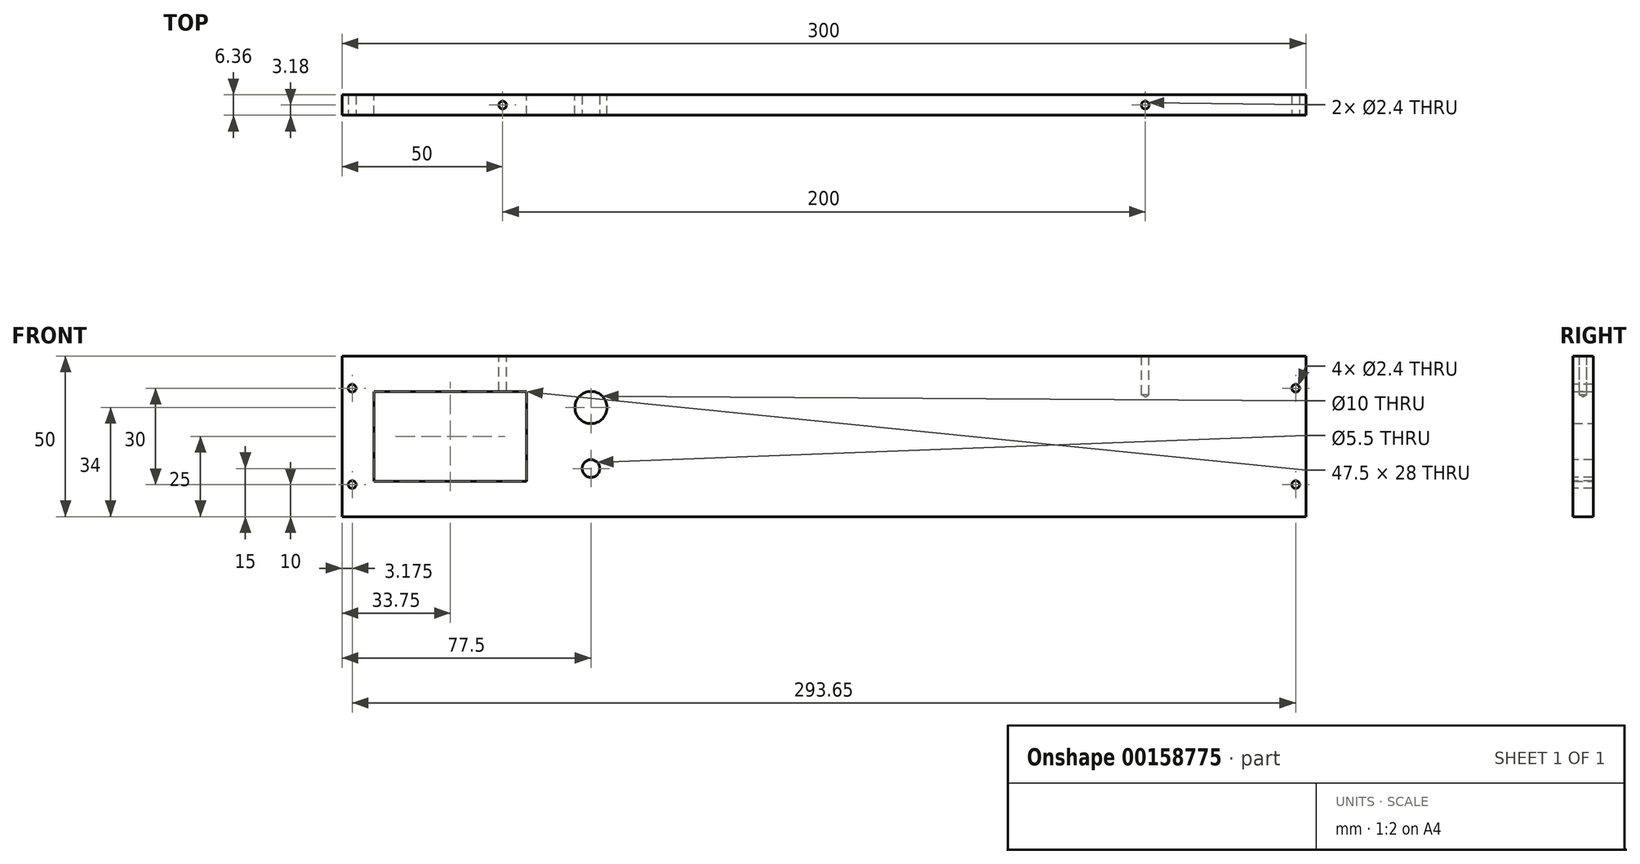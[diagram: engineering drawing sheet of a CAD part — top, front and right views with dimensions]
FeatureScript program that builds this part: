
annotation { "Feature Type Name" : "Feature", "Feature Type Description" : "" }
export const myFeature = defineFeature(function(context is Context, id is Id, definition is map)
    precondition{}
    {
        {
            var Q0;
            Q0=qCreatedBy(makeId("Front.planeOp"),FACE);
            var sketch = newSketch(context, id + "F0", { "sketchPlane" : qUnion([Q0])});
            skLineSegment(sketch, "E0.bottom", {"start": v(150, -25) * mm, "end": v(-150, -25) * mm});
            skLineSegment(sketch, "E0.top", {"start": v(150, 25) * mm, "end": v(-150, 25) * mm});
            skLineSegment(sketch, "E0.left", {"start": v(150, -25) * mm, "end": v(150, 25) * mm});
            skLineSegment(sketch, "E0.right", {"start": v(-150, -25) * mm, "end": v(-150, 25) * mm});
            skPoint(sketch, "E0.middle", {"position": v(0, 0) * mm});
            skLineSegment(sketch, "E1.bottom", {"start": v(-92.5, -14) * mm, "end": v(-140, -14) * mm});
            skLineSegment(sketch, "E1.top", {"start": v(-92.5, 14) * mm, "end": v(-140, 14) * mm});
            skLineSegment(sketch, "E1.left", {"start": v(-92.5, -14) * mm, "end": v(-92.5, 14) * mm});
            skLineSegment(sketch, "E1.right", {"start": v(-140, -14) * mm, "end": v(-140, 14) * mm});
            skPoint(sketch, "E1.middle", {"position": v(-116.25, 0) * mm});
            skCircle(sketch, "E2", {"center": v(-72.5, 9) * mm, "radius": 5 * mm});
            skSolve(sketch);
        }
        {
            var Q0;
            Q0=qSketchRegion(id+"F0",true);
            extrude(context, id + "F1", {"entities" : qUnion([Q0]), "endBound" : BoundingType.SYMMETRIC, "depth" : 6.35 * mm});
        }
        {
            var Q0;
            Q0=makeQuery(id+"F1.opExtrude","CAP_FACE",FACE,{"disambiguationData":[OSD([sQuery(id+"F0.wireOp",EDGE,"E0.bottom"),sQuery(id+"F0.wireOp",EDGE,"E0.top"),sQuery(id+"F0.wireOp",EDGE,"E0.left"),sQuery(id+"F0.wireOp",EDGE,"E0.right")])],"isStart":false});
            var sketch = newSketch(context, id + "F2", { "sketchPlane" : qUnion([Q0])});
            skCircle(sketch, "E3", {"center": v(-146.82, -15) * mm, "radius": 1.5 * mm});
            skCircle(sketch, "E4.MirrorC", {"center": v(146.82, -15) * mm, "radius": 1.5 * mm});
            skCircle(sketch, "E5.MirrorC", {"center": v(-146.82, 15) * mm, "radius": 1.5 * mm});
            skCircle(sketch, "E6.MirrorC", {"center": v(146.82, 15) * mm, "radius": 1.5 * mm});
            skSolve(sketch);
        }
        {
            var Q0;
            Q0=sQuery(id+"F2.wireOp",VERTEX,"E5.MirrorC.center");
            var Q1;
            Q1=sQuery(id+"F2.wireOp",VERTEX,"E3.center");
            var Q2;
            Q2=sQuery(id+"F2.wireOp",VERTEX,"E6.MirrorC.center");
            var Q3;
            Q3=sQuery(id+"F2.wireOp",VERTEX,"E4.MirrorC.center");
            var Q4;
            Q4=makeQuery(id+"F1.opExtrude","SWEPT_BODY",BODY,{"disambiguationData":[OSD([sQuery(id+"F0.wireOp",EDGE,"E0.bottom"),sQuery(id+"F0.wireOp",EDGE,"E0.top"),sQuery(id+"F0.wireOp",EDGE,"E0.left"),sQuery(id+"F0.wireOp",EDGE,"E0.right")])]});
            hole(context, id + "F3", {"style" : HoleStyle.SIMPLE, "endStyle" : HoleEndStyle.THROUGH, "holeDiameter" : 2.4 * mm, "locations" : qUnion([Q0, Q1, Q2, Q3]), "scope" : qUnion([Q4]), "isTappedThrough" : true});
        }
        {
            var Q0;
            Q0=makeQuery(id+"F1.opExtrude","SWEPT_FACE",FACE,{"disambiguationData":[OSD([sQuery(id+"F0.wireOp",EDGE,"E0.top")])]});
            var sketch = newSketch(context, id + "F4", { "sketchPlane" : qUnion([Q0])});
            skCircle(sketch, "E7", {"center": v(-100, 0) * mm, "radius": 1.5 * mm});
            skCircle(sketch, "E8.MirrorC", {"center": v(100, 0) * mm, "radius": 1.5 * mm});
            skSolve(sketch);
        }
        {
            var Q0;
            Q0=sQuery(id+"F4.wireOp",VERTEX,"E7.center");
            var Q1;
            Q1=sQuery(id+"F4.wireOp",VERTEX,"E8.MirrorC.center");
            var Q2;
            Q2=makeQuery(id+"F1.opExtrude","SWEPT_BODY",BODY,{"disambiguationData":[OSD([sQuery(id+"F0.wireOp",EDGE,"E0.bottom"),sQuery(id+"F0.wireOp",EDGE,"E0.top"),sQuery(id+"F0.wireOp",EDGE,"E0.left"),sQuery(id+"F0.wireOp",EDGE,"E0.right")])]});
            hole(context, id + "F5", {"style" : HoleStyle.SIMPLE, "endStyle" : HoleEndStyle.BLIND, "standardTappedOrClearance" : lookupTablePath({ "standard" : "ISO", "engagement" : "75%", "pitch" : "0.6 mm", "size" : "M3", "type" : "Tapped" }), "standardBlindInLast" : lookupTablePath({ "standard" : "ISO", "engagement" : "75%", "pitch" : "0.6 mm", "size" : "M3", "type" : "Tapped" }), "holeDiameter" : 2.4 * mm, "holeDepth" : 12 * mm, "locations" : qUnion([Q0, Q1]), "scope" : qUnion([Q2])});
        }
        {
            var Q0;
            Q0=makeQuery(id+"F1.opExtrude","CAP_FACE",FACE,{"disambiguationData":[OSD([sQuery(id+"F0.wireOp",EDGE,"E0.bottom"),sQuery(id+"F0.wireOp",EDGE,"E0.top"),sQuery(id+"F0.wireOp",EDGE,"E0.left"),sQuery(id+"F0.wireOp",EDGE,"E0.right"),sQuery(id+"F0.wireOp",EDGE,"E1.bottom"),sQuery(id+"F0.wireOp",EDGE,"E1.top"),sQuery(id+"F0.wireOp",EDGE,"E1.left"),sQuery(id+"F0.wireOp",EDGE,"E1.right"),sQuery(id+"F0.wireOp",EDGE,"E2")])],"isStart":false});
            var sketch = newSketch(context, id + "F6", { "sketchPlane" : qUnion([Q0])});
            skCircle(sketch, "E9", {"center": v(-72.5, -10) * mm, "radius": 2.5 * mm});
            skSolve(sketch);
        }
        {
            var Q0;
            Q0=sQuery(id+"F6.wireOp",VERTEX,"E9.center");
            var Q1;
            Q1=makeQuery(id+"F1.opExtrude","SWEPT_BODY",BODY,{"disambiguationData":[OSD([sQuery(id+"F0.wireOp",EDGE,"E0.bottom"),sQuery(id+"F0.wireOp",EDGE,"E0.top"),sQuery(id+"F0.wireOp",EDGE,"E0.left"),sQuery(id+"F0.wireOp",EDGE,"E0.right"),sQuery(id+"F0.wireOp",EDGE,"E1.bottom"),sQuery(id+"F0.wireOp",EDGE,"E1.top"),sQuery(id+"F0.wireOp",EDGE,"E1.left"),sQuery(id+"F0.wireOp",EDGE,"E1.right"),sQuery(id+"F0.wireOp",EDGE,"E2")])]});
            hole(context, id + "F7", {"style" : HoleStyle.SIMPLE, "endStyle" : HoleEndStyle.THROUGH, "standardTappedOrClearance" : lookupTablePath({ "standard" : "ISO", "fit" : "Normal", "size" : "M5", "type" : "Clearance" }), "standardBlindInLast" : lookupTablePath({ "fit" : "Standard", "standard" : "ISO", "size" : "M5", "type" : "Clearance" }), "holeDiameter" : 5.5 * mm, "locations" : qUnion([Q0]), "scope" : qUnion([Q1]), "isTappedThrough" : true});
        }
    });
